# Revit family: Electronics_Masking-Generators_Biamp_Cambridge_Networked-Sound-Masking-Processor_DS3002__
name_source: partatom
category: Communication Devices
units: mm (PartAtom-declared; Revit-internal decimal feet)

## family parameters
Cut with Voids When Loaded = No
Host = Face
Maintain Annotation Orientation = No
OmniClass Number = 23.85.10.11.11
OmniClass Title = Sound and Signal Devices
Part Type = Normal
Room Calculation Point = No
Round Connector Dimension = Use Diameter
Shared = No

## types (1)
- DS3002
    Altitude = 0-6,600 ft (0-2000m) MSL
    Apparent Load = 0 VA
    Compliance = ETL listed (USA)
    Connector = DS-CP8200
    Connector Description = 120VAC 50/60Hz
    Default Elevation = 48 "
    Depth = 8 "
    Description = Dynasound® DS3002 Networked Sound Masking, Paging and Music Processor
    Frequency Response Music/Paging = 20Hz to 20kHz
    Frequency Response Sound Masking = 100Hz to 10kHz
    Function = Optional via Software
    Height = 1.75 "
    Housing Material = Biamp - Plastic - Black
    Humidity = 0-95% relative humidity (non-condensing)
    Included Accessories = Ethernet Crossover Cable
    Input Connector Type = Captive Screw Terminal
    Input Impedance = 20kΩ balanced / 10kΩ unbalanced
    Input Level = Line Level
    Manufacturer = Biamp
    Masking Level Adjustment = via Privacy Manager Software
    Max Power Consumption = 0 W
    Maximum Power Consumption = 22W
    Model = DS3002
    Network Connection = RJ-45 with Ethernet cable (Cat 5e and above)
    Nominal Output Impedance = 150Ω
    Number of Inputs = 2 (Mono)
    Number of Masking Zones = Up to 2
    Number of Non-Correlated Masking Sources = 4
    Number of Outputs = 2 (Mono)
    Number of Poles = 1
    Output Connector Type = Captive Screw Terminal
    Output Level = Line Level
    Power Factor = 1
    Product Documentation Link = https://downloads.biamp.com
    Product Page URL = https://www.biamp.com
    Product data url = https://www.bimobject.com
    Sound Masking Equalization = 1/3 Octave Bands
    Temperature Range = 14 - 104° F (-10 – 40° C)
    URL = https://www.biamp.com
    Voltage = 120 V
    Weight = 6.00 lbf
    Width = 19 "

## geometry (parser evidence)
native form markers: Sweep x4
no freeform markers — native parametric forms only
